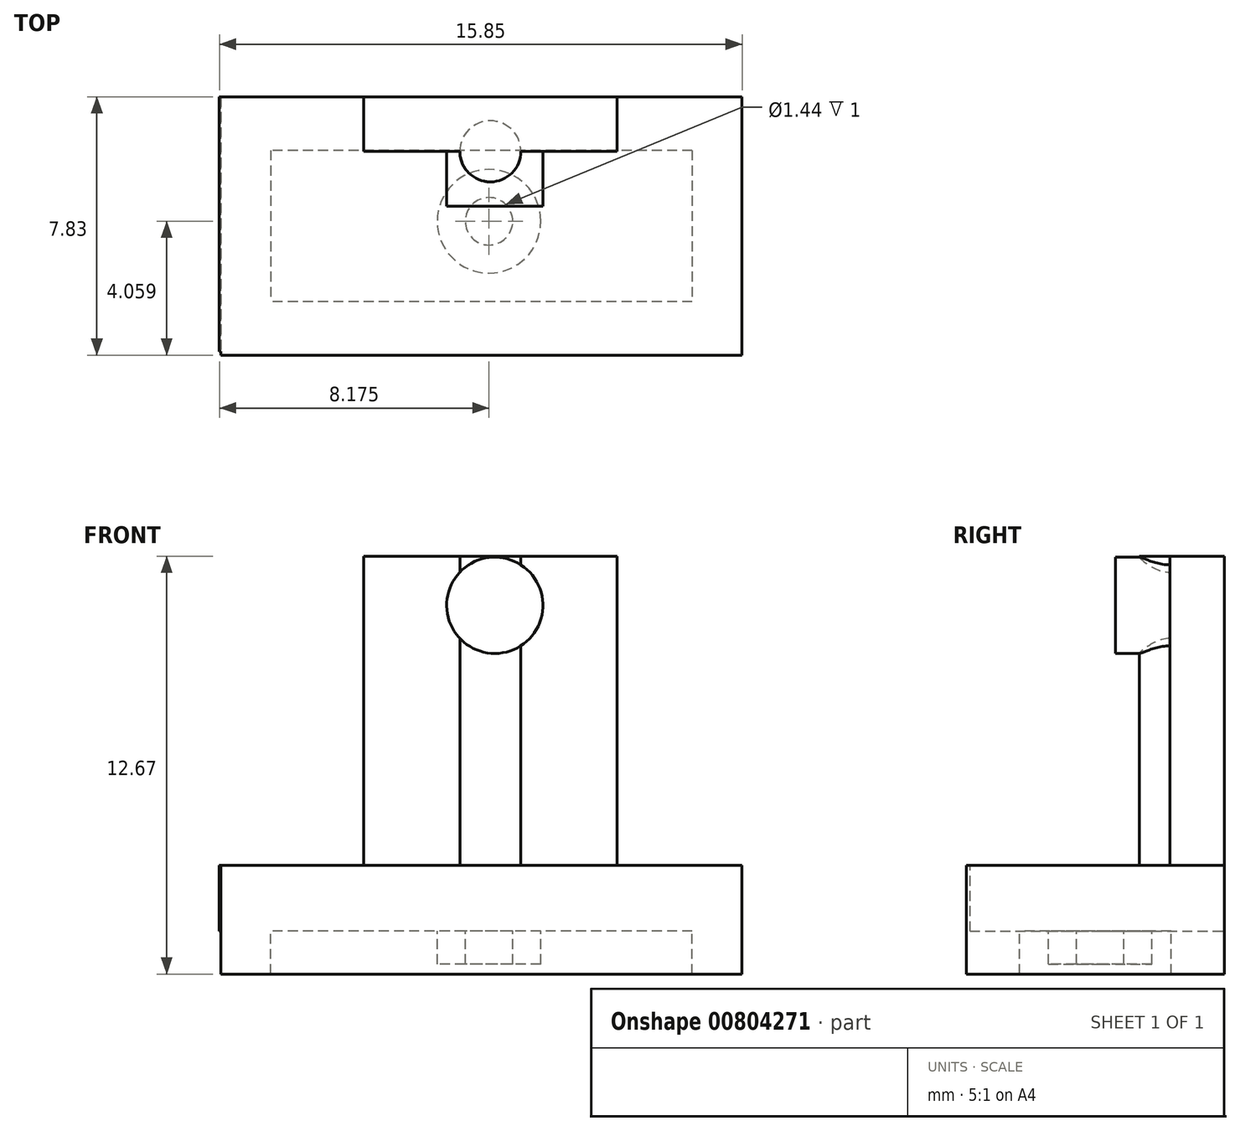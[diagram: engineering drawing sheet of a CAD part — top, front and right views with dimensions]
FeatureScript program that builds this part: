
annotation { "Feature Type Name" : "Feature", "Feature Type Description" : "" }
export const myFeature = defineFeature(function(context is Context, id is Id, definition is map)
    precondition{}
    {
        {
            var Q0;
            Q0=qCreatedBy(makeId("Top.planeOp"),FACE);
            var sketch = newSketch(context, id + "F0", { "sketchPlane" : qUnion([Q0])});
            skLineSegment(sketch, "E0.bottom", {"start": v(-8.6, 0) * mm, "end": v(7.2, 0) * mm});
            skLineSegment(sketch, "E0.top", {"start": v(-8.6, -7.83) * mm, "end": v(7.2, -7.83) * mm});
            skLineSegment(sketch, "E0.left", {"start": v(-8.6, 0) * mm, "end": v(-8.6, -7.83) * mm});
            skLineSegment(sketch, "E0.right", {"start": v(7.2, 0) * mm, "end": v(7.2, -7.83) * mm});
            skSolve(sketch);
        }
        {
            var Q0;
            Q0 = qSketchRegion(id + "F0", true);
            extrude(context, id + "F1", {"entities" : qUnion([Q0]), "oppositeDirection" : true, "depth" : 3.3 * mm, "offsetDistance" : 25 * mm});
        }
        {
            var Q0;
            Q0=qCreatedBy(makeId("Top.planeOp"),FACE);
            var sketch = newSketch(context, id + "F2", { "sketchPlane" : qUnion([Q0])});
            skLineSegment(sketch, "E1.bottom", {"start": v(-4.27, 0) * mm, "end": v(3.4, 0) * mm});
            skLineSegment(sketch, "E1.top", {"start": v(-4.27, -1.65) * mm, "end": v(3.4, -1.65) * mm});
            skLineSegment(sketch, "E1.left", {"start": v(-4.27, 0) * mm, "end": v(-4.27, -1.65) * mm});
            skLineSegment(sketch, "E1.right", {"start": v(3.4, 0) * mm, "end": v(3.4, -1.65) * mm});
            skCircle(sketch, "E2", {"center": v(-0.43, -1.65) * mm, "radius": 0.93 * mm});
            skSolve(sketch);
        }
        {
            var Q0;
            Q0 = qSketchRegion(id + "F2", true);
            extrude(context, id + "F3", {"entities" : qUnion([Q0]), "operationType" : NewBodyOperationType.ADD, "depth" : 9.37 * mm, "offsetDistance" : 25 * mm});
        }
        {
            var Q0;
            Q0=qCreatedBy(makeId("Front.planeOp"),FACE);
            var sketch = newSketch(context, id + "F4", { "sketchPlane" : qUnion([Q0])});
            skCircle(sketch, "E3", {"center": v(-0.3, 7.88) * mm, "radius": 1.46 * mm});
            skSolve(sketch);
        }
        {
            var Q0;
            Q0 = qSketchRegion(id + "F4", true);
            extrude(context, id + "F5", {"entities" : qUnion([Q0]), "operationType" : NewBodyOperationType.ADD, "depth" : 3.31 * mm, "offsetDistance" : 25 * mm});
        }
        {
            var Q0;
            Q0=qCreatedBy(makeId("Top.planeOp"),FACE);
            var sketch = newSketch(context, id + "F6", { "sketchPlane" : qUnion([Q0])});
            skLineSegment(sketch, "E4.bottom", {"start": v(-7.1, -6.2) * mm, "end": v(5.69, -6.2) * mm});
            skLineSegment(sketch, "E4.top", {"start": v(-7.1, -1.62) * mm, "end": v(5.69, -1.62) * mm});
            skLineSegment(sketch, "E4.left", {"start": v(-7.1, -6.2) * mm, "end": v(-7.1, -1.62) * mm});
            skLineSegment(sketch, "E4.right", {"start": v(5.69, -6.2) * mm, "end": v(5.69, -1.62) * mm});
            skSolve(sketch);
        }
        {
            var Q0;
            Q0 = qSketchRegion(id + "F6", true);
            extrude(context, id + "F7", {"entities" : qUnion([Q0]), "operationType" : NewBodyOperationType.REMOVE, "oppositeDirection" : true, "depth" : 25 * mm, "offsetDistance" : 25 * mm});
        }
        {
            var Q0;
            Q0=qCreatedBy(makeId("Top.planeOp"),FACE);
            var sketch = newSketch(context, id + "F8", { "sketchPlane" : qUnion([Q0])});
            skLineSegment(sketch, "E5.bottom", {"start": v(-8.65, 0) * mm, "end": v(7.14, 0) * mm});
            skLineSegment(sketch, "E5.top", {"start": v(-8.65, -7.71) * mm, "end": v(7.14, -7.71) * mm});
            skLineSegment(sketch, "E5.left", {"start": v(-8.65, 0) * mm, "end": v(-8.65, -7.71) * mm});
            skLineSegment(sketch, "E5.right", {"start": v(7.14, 0) * mm, "end": v(7.14, -7.71) * mm});
            skSolve(sketch);
        }
        {
            var Q0;
            Q0 = qSketchRegion(id + "F8", true);
            extrude(context, id + "F9", {"entities" : qUnion([Q0]), "operationType" : NewBodyOperationType.ADD, "oppositeDirection" : true, "depth" : 2 * mm, "offsetDistance" : 25 * mm});
        }
        {
            var Q0;
            Q0=qCreatedBy(makeId("Top.planeOp"),FACE);
            var sketch = newSketch(context, id + "F10", { "sketchPlane" : qUnion([Q0])});
            skCircle(sketch, "E6", {"center": v(-0.47, -3.77) * mm, "radius": 1.57 * mm});
            skCircle(sketch, "E7", {"center": v(-0.47, -3.77) * mm, "radius": 0.72 * mm});
            skSolve(sketch);
        }
        {
            var Q0;
            Q0 = qSketchRegion(id + "F10", true);
            extrude(context, id + "F11", {"entities" : qUnion([Q0]), "operationType" : NewBodyOperationType.ADD, "oppositeDirection" : true, "depth" : 3 * mm, "offsetDistance" : 25 * mm});
        }
    });
